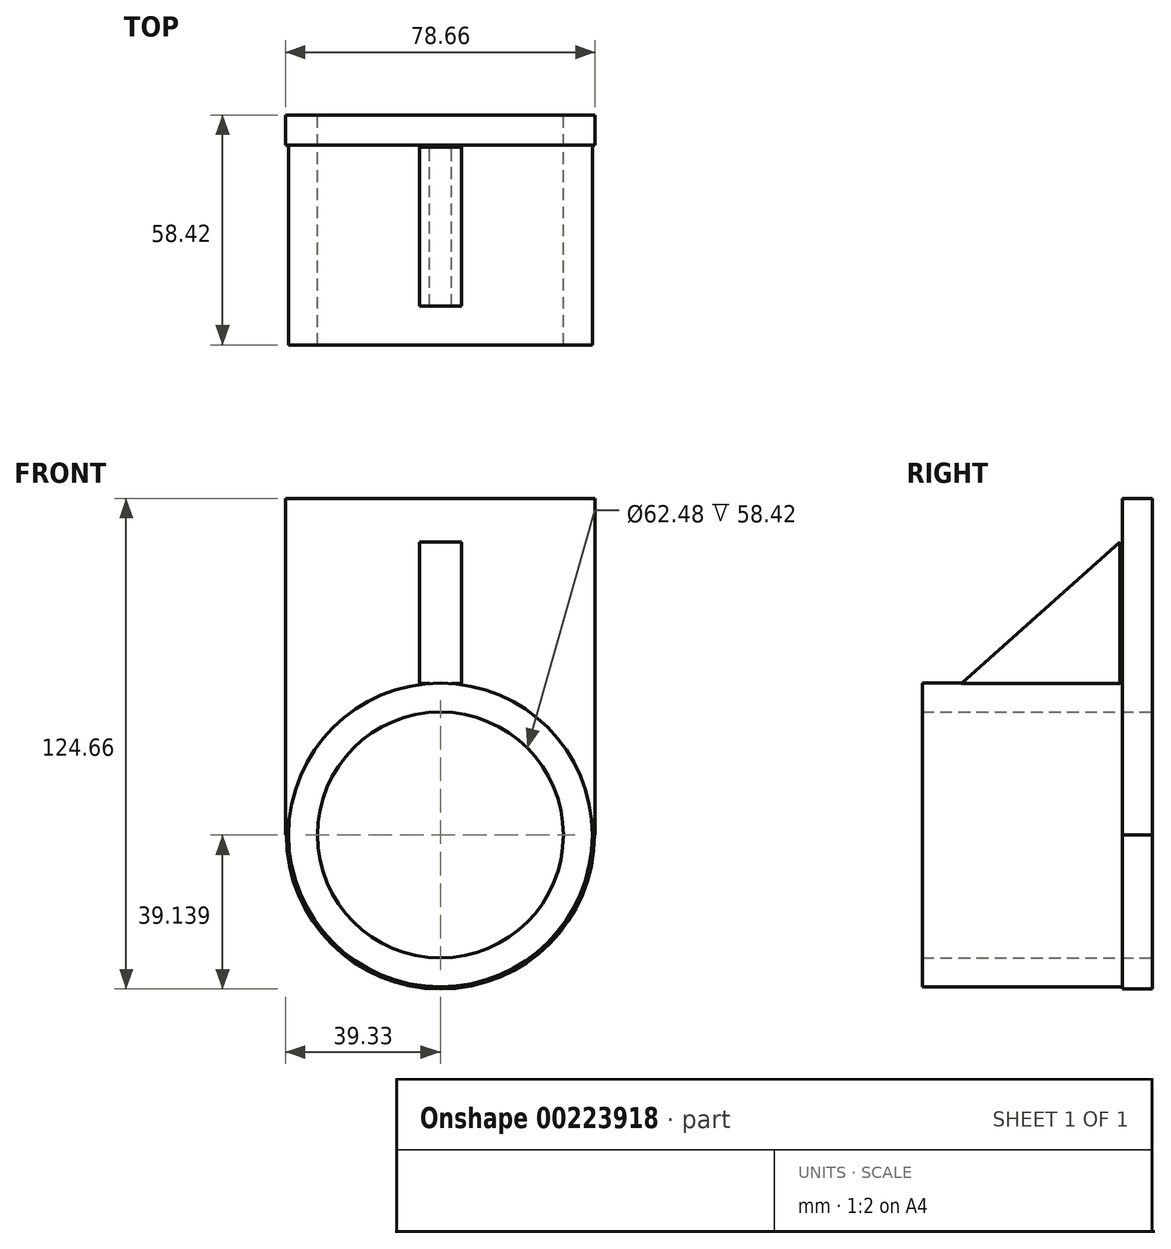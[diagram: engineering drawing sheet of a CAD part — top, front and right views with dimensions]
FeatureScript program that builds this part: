
annotation { "Feature Type Name" : "Feature", "Feature Type Description" : "" }
export const myFeature = defineFeature(function(context is Context, id is Id, definition is map)
    precondition{}
    {
        {
            var Q0;
            Q0=qCreatedBy(makeId("Front.planeOp"),FACE);
            var sketch = newSketch(context, id + "F0", { "sketchPlane" : qUnion([Q0])});
            skLineSegment(sketch, "E0.bottom", {"start": v(39.33, 42.76) * mm, "end": v(-39.33, 42.76) * mm});
            skLineSegment(sketch, "E0.top", {"start": v(39.33, -42.76) * mm, "end": v(-39.33, -42.76) * mm});
            skLineSegment(sketch, "E0.left", {"start": v(39.33, 42.76) * mm, "end": v(39.33, -42.76) * mm});
            skLineSegment(sketch, "E0.right", {"start": v(-39.33, 42.76) * mm, "end": v(-39.33, -42.76) * mm});
            skPoint(sketch, "E0.middle", {"position": v(0, 0) * mm});
            skLineSegment(sketch, "E1.left", {"start": v(39.33, -13.86) * mm, "end": v(39.33, -42.76) * mm});
            skLineSegment(sketch, "E1.right", {"start": v(-39.33, -13.86) * mm, "end": v(-39.33, -42.76) * mm});
            skPoint(sketch, "E1.middle", {"position": v(0, -42.76) * mm});
            skCircle(sketch, "E2", {"center": v(0, -42.76) * mm, "radius": 39.13 * mm});
            skCircle(sketch, "E3", {"center": v(0, -42.76) * mm, "radius": 31.24 * mm});
            skPoint(sketch, "E4.orphan", {"position": v(-39.33, -71.67) * mm});
            skPoint(sketch, "E5.orphan", {"position": v(39.33, -71.67) * mm});
            skSolve(sketch);
        }
        {
            var Q0;
            Q0 = qSketchRegion(id + "F0", true);
            extrude(context, id + "F1", {"entities" : qUnion([Q0]), "depth" : 7.62 * mm});
        }
        {
            var Q0;
            Q0=makeQuery(id+"F1.opExtrude","CAP_FACE",FACE,{"disambiguationData":[OSD([sQuery(id+"F0.wireOp",EDGE,"E0.bottom"),sQuery(id+"F0.wireOp",EDGE,"E0.top"),sQuery(id+"F0.wireOp",EDGE,"E0.left"),sQuery(id+"F0.wireOp",EDGE,"E0.right"),sQuery(id+"F0.wireOp",EDGE,"E1.left"),sQuery(id+"F0.wireOp",EDGE,"E1.right"),sQuery(id+"F0.wireOp",EDGE,"E2"),sQuery(id+"F0.wireOp",EDGE,"E3")])],"isStart":false});
            var sketch = newSketch(context, id + "F2", { "sketchPlane" : qUnion([Q0])});
            skCircle(sketch, "E6", {"center": v(0, -42.76) * mm, "radius": 38.59 * mm});
            skCircle(sketch, "E7", {"center": v(0, -42.76) * mm, "radius": 31.03 * mm});
            skSolve(sketch);
        }
        {
            var Q0;
            Q0=makeQuery(id+"F2.imprint","IMPRINT",FACE,{"disambiguationData":[TD([[makeQuery(id+"F2.imprint","IMPRINT",EDGE,{"derivedFrom":sQuery(id+"F2.wireOp",EDGE,"E6")}),1.0]])]});
            extrude(context, id + "F3", {"entities" : qUnion([Q0]), "operationType" : NewBodyOperationType.ADD, "depth" : 50.8 * mm});
        }
        {
            var Q0;
            Q0=qCreatedBy(makeId("Right.planeOp"),FACE);
            var sketch = newSketch(context, id + "F4", { "sketchPlane" : qUnion([Q0])});
            skLineSegment(sketch, "E8.bottom", {"start": v(-8.18, -4.27) * mm, "end": v(-48.49, -4.27) * mm});
            skLineSegment(sketch, "E8.top", {"start": v(-8.18, 31.66) * mm, "end": v(-48.49, 31.66) * mm});
            skLineSegment(sketch, "E8.left", {"start": v(-8.18, -4.27) * mm, "end": v(-8.18, 31.66) * mm});
            skLineSegment(sketch, "E8.right", {"start": v(-48.49, -4.27) * mm, "end": v(-48.49, 31.66) * mm});
            skSolve(sketch);
        }
        {
            var Q0;
            Q0 = qSketchRegion(id + "F4", true);
            extrude(context, id + "F5", {"entities" : qUnion([Q0]), "operationType" : NewBodyOperationType.ADD, "endBound" : BoundingType.SYMMETRIC, "depth" : 10.67 * mm});
        }
        {
            var Q0;
            Q0=makeQuery(id+"F5.opExtrude","CAP_FACE",FACE,{"disambiguationData":[OSD([sQuery(id+"F4.wireOp",EDGE,"E8.bottom"),sQuery(id+"F4.wireOp",EDGE,"E8.top"),sQuery(id+"F4.wireOp",EDGE,"E8.left"),sQuery(id+"F4.wireOp",EDGE,"E8.right")])],"isStart":false});
            var sketch = newSketch(context, id + "F6", { "sketchPlane" : qUnion([Q0])});
            skLineSegment(sketch, "E9", {"start": v(-48.49, -4.27) * mm, "end": v(-8.18, 31.66) * mm});
            skLineSegment(sketch, "E10", {"start": v(-8.18, 31.66) * mm, "end": v(-48.49, 31.66) * mm});
            skLineSegment(sketch, "E11", {"start": v(-48.49, 31.66) * mm, "end": v(-48.49, -4.27) * mm});
            skSolve(sketch);
        }
        {
            var Q0;
            Q0 = qSketchRegion(id + "F6", true);
            extrude(context, id + "F7", {"entities" : qUnion([Q0]), "operationType" : NewBodyOperationType.REMOVE, "endBound" : BoundingType.THROUGH_ALL, "oppositeDirection" : true, "depth" : 25.4 * mm});
        }
    });
